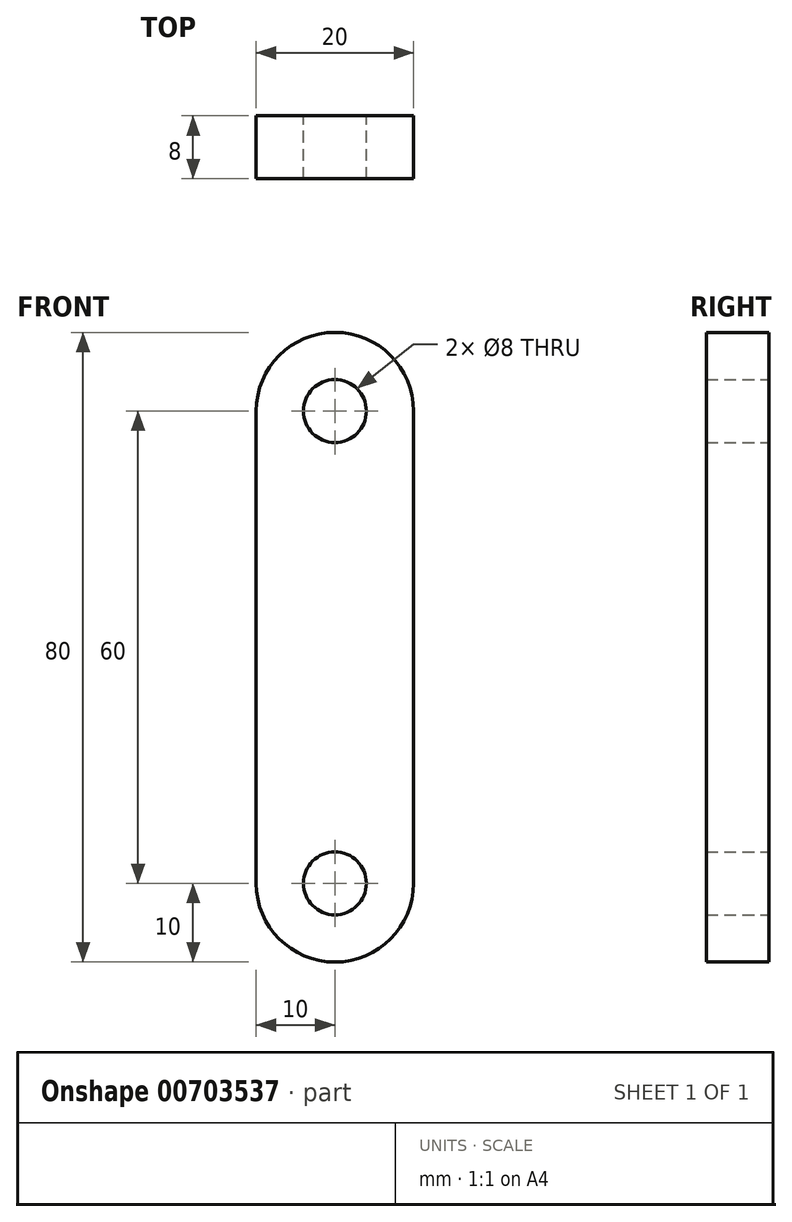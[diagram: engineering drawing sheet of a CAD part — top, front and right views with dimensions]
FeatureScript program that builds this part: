
annotation { "Feature Type Name" : "Feature", "Feature Type Description" : "" }
export const myFeature = defineFeature(function(context is Context, id is Id, definition is map)
    precondition{}
    {
        {
            var Q0;
            Q0=qCreatedBy(makeId("Front.planeOp"),FACE);
            var sketch = newSketch(context, id + "F0", { "sketchPlane" : qUnion([Q0])});
            skLineSegment(sketch, "E0.bottom", {"start": v(-10, 0) * mm, "end": v(10, 0) * mm});
            skLineSegment(sketch, "E0.left", {"start": v(-10, 0) * mm, "end": v(-10, 30) * mm});
            skLineSegment(sketch, "E0.right", {"start": v(10, 0) * mm, "end": v(10, 30) * mm});
            skArc(sketch, "E1", {"start": v(-10, 30) * mm, "mid": v(0, 40) * mm, "end": v(10, 30) * mm});
            skCircle(sketch, "E2", {"center": v(0, 30) * mm, "radius": 4 * mm});
            skLineSegment(sketch, "E3.MirrorCS", {"start": v(10, 0) * mm, "end": v(10, -30) * mm});
            skCircle(sketch, "E4.MirrorC", {"center": v(0, -30) * mm, "radius": 4 * mm});
            skArc(sketch, "E5.MirrorCS", {"start": v(-10, -30) * mm, "mid": v(0, -40) * mm, "end": v(10, -30) * mm});
            skLineSegment(sketch, "E6.MirrorCS", {"start": v(-10, 0) * mm, "end": v(-10, -30) * mm});
            skSolve(sketch);
        }
        {
            var Q0;
            Q0=makeQuery(id+"F0.imprint","IMPRINT",FACE,{"disambiguationData":[TD([[makeQuery(id+"F0.imprint","IMPRINT",EDGE,{"derivedFrom":sQuery(id+"F0.wireOp",EDGE,"E0.bottom")}),1.0]])]});
            var Q1;
            Q1=makeQuery(id+"F0.imprint","IMPRINT",FACE,{"disambiguationData":[TD([[makeQuery(id+"F0.imprint","IMPRINT",EDGE,{"derivedFrom":sQuery(id+"F0.wireOp",EDGE,"E0.bottom")}),-1.0]])]});
            extrude(context, id + "F1", {"entities" : qUnion([Q0, Q1]), "depth" : 8 * mm, "offsetDistance" : 25 * mm});
        }
    });
